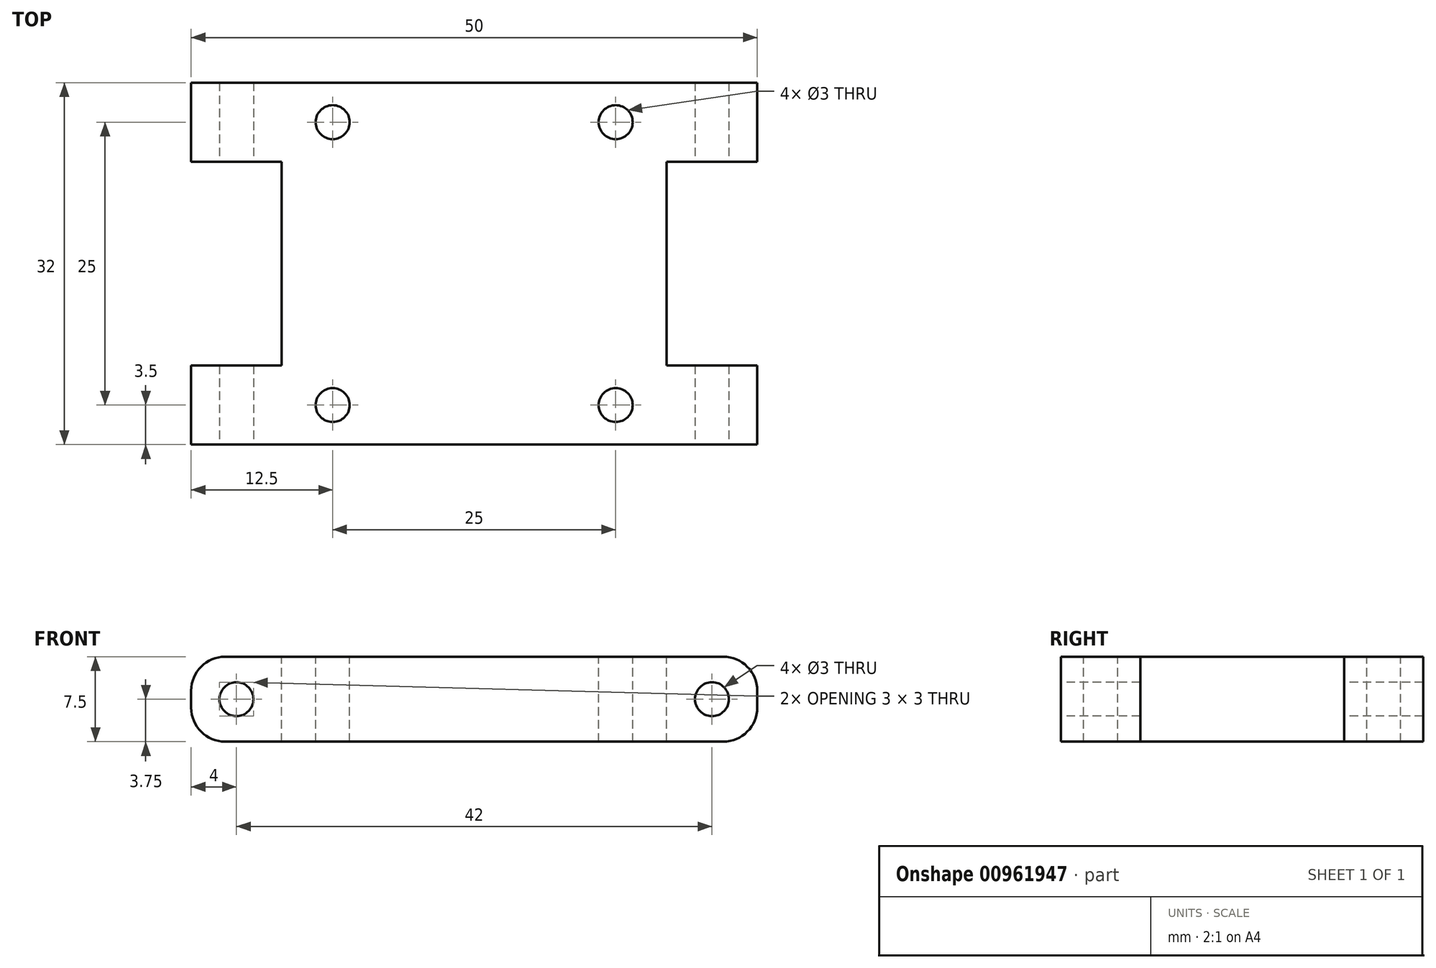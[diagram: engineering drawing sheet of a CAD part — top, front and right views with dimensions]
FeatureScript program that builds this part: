
annotation { "Feature Type Name" : "Feature", "Feature Type Description" : "" }
export const myFeature = defineFeature(function(context is Context, id is Id, definition is map)
    precondition{}
    {
        {
            var Q0;
            Q0=qCreatedBy(makeId("Top.planeOp"),FACE);
            var sketch = newSketch(context, id + "F0", { "sketchPlane" : qUnion([Q0])});
            skLineSegment(sketch, "E0.bottom", {"start": v(0, 0) * mm, "end": v(25, 0) * mm});
            skLineSegment(sketch, "E0.top", {"start": v(0, 32) * mm, "end": v(25, 32) * mm});
            skLineSegment(sketch, "E0.left", {"start": v(0, 0) * mm, "end": v(0, 32) * mm});
            skLineSegment(sketch, "E0.right", {"start": v(25, 0) * mm, "end": v(25, 32) * mm});
            skSolve(sketch);
        }
        {
            var Q0;
            Q0=makeQuery(id+"F0.imprint","IMPRINT",FACE,{"disambiguationData":[TD([[makeQuery(id+"F0.imprint","IMPRINT",EDGE,{"derivedFrom":sQuery(id+"F0.wireOp",EDGE,"E0.bottom")}),1.0]])]});
            extrude(context, id + "F1", {"entities" : qUnion([Q0]), "depth" : 7.5 * mm, "offsetDistance" : 25 * mm, "symmetric" : true});
        }
        {
            var Q0;
            Q0=qCreatedBy(makeId("Top.planeOp"),FACE);
            var sketch = newSketch(context, id + "F2", { "sketchPlane" : qUnion([Q0])});
            skLineSegment(sketch, "E1.bottom", {"start": v(29.2, 25) * mm, "end": v(17, 25) * mm});
            skLineSegment(sketch, "E1.top", {"start": v(29.2, 7) * mm, "end": v(17, 7) * mm});
            skLineSegment(sketch, "E1.left", {"start": v(29.2, 25) * mm, "end": v(29.2, 7) * mm});
            skLineSegment(sketch, "E1.right", {"start": v(17, 25) * mm, "end": v(17, 7) * mm});
            skSolve(sketch);
        }
        {
            var Q0;
            Q0=makeQuery(id+"F2.imprint","IMPRINT",FACE,{"disambiguationData":[TD([[makeQuery(id+"F2.imprint","IMPRINT",EDGE,{"derivedFrom":sQuery(id+"F2.wireOp",EDGE,"E1.bottom")}),1.0]])]});
            extrude(context, id + "F3", {"entities" : qUnion([Q0]), "operationType" : NewBodyOperationType.REMOVE, "oppositeDirection" : true, "depth" : 7.5 * mm, "offsetDistance" : 25 * mm, "symmetric" : true});
        }
        {
            var Q0;
            Q0=qCreatedBy(makeId("Front.planeOp"),FACE);
            var sketch = newSketch(context, id + "F4", { "sketchPlane" : qUnion([Q0])});
            skCircle(sketch, "E2", {"center": v(21, 0) * mm, "radius": 1.5 * mm});
            skSolve(sketch);
        }
        {
            var Q0;
            Q0=makeQuery(id+"F4.imprint","IMPRINT",FACE,{"disambiguationData":[TD([[makeQuery(id+"F4.imprint","IMPRINT",EDGE,{"derivedFrom":sQuery(id+"F4.wireOp",EDGE,"E2")}),1.0]])]});
            extrude(context, id + "F5", {"entities" : qUnion([Q0]), "operationType" : NewBodyOperationType.REMOVE, "oppositeDirection" : true, "depth" : 32 * mm, "offsetDistance" : 25 * mm});
        }
        {
            var Q0;
            {var subQ0=sQuery(id+"F0.wireOp",EDGE,"E0.right");var subQ1=sQuery(id+"F0.wireOp",EDGE,"E0.top");Q0=makeQuery(id+"F3.boolean.opBoolean","SPLIT",EDGE,{"disambiguationData":[TD([makeQuery(id+"F1.opExtrude","SWEPT_FACE",FACE,{"disambiguationData":[OSD([subQ1])]})])],"derivedFrom":makeQuery(id+"F1.opExtrude","CAP_EDGE",EDGE,{"disambiguationData":[OSD([subQ0])],"isStart":true})});}
            var Q1;
            {var subQ0=sQuery(id+"F0.wireOp",EDGE,"E0.right");var subQ1=sQuery(id+"F0.wireOp",EDGE,"E0.top");Q1=makeQuery(id+"F3.boolean.opBoolean","SPLIT",EDGE,{"disambiguationData":[TD([makeQuery(id+"F1.opExtrude","SWEPT_FACE",FACE,{"disambiguationData":[OSD([subQ1])]})])],"derivedFrom":makeQuery(id+"F1.opExtrude","CAP_EDGE",EDGE,{"disambiguationData":[OSD([subQ0])],"isStart":false})});}
            var Q2;
            {var subQ0=sQuery(id+"F0.wireOp",EDGE,"E0.bottom");var subQ1=sQuery(id+"F0.wireOp",EDGE,"E0.right");Q2=makeQuery(id+"F3.boolean.opBoolean","SPLIT",EDGE,{"disambiguationData":[TD([makeQuery(id+"F1.opExtrude","SWEPT_FACE",FACE,{"disambiguationData":[OSD([subQ0])]})])],"derivedFrom":makeQuery(id+"F1.opExtrude","CAP_EDGE",EDGE,{"disambiguationData":[OSD([subQ1])],"isStart":false})});}
            var Q3;
            {var subQ0=sQuery(id+"F0.wireOp",EDGE,"E0.bottom");var subQ1=sQuery(id+"F0.wireOp",EDGE,"E0.right");Q3=makeQuery(id+"F3.boolean.opBoolean","SPLIT",EDGE,{"disambiguationData":[TD([makeQuery(id+"F1.opExtrude","SWEPT_FACE",FACE,{"disambiguationData":[OSD([subQ0])]})])],"derivedFrom":makeQuery(id+"F1.opExtrude","CAP_EDGE",EDGE,{"disambiguationData":[OSD([subQ1])],"isStart":true})});}
            fillet(context, id + "F6", {"entities" : qUnion([Q0, Q1, Q2, Q3]), "radius" : 3 * mm, "tangentPropagation" : true, "allowEdgeOverflow" : false});
        }
        {
            var Q0;
            Q0=qCreatedBy(makeId("Top.planeOp"),FACE);
            var sketch = newSketch(context, id + "F7", { "sketchPlane" : qUnion([Q0])});
            skCircle(sketch, "E3", {"center": v(12.5, 3.5) * mm, "radius": 1.5 * mm});
            skCircle(sketch, "E4", {"center": v(12.5, 28.5) * mm, "radius": 1.5 * mm});
            skSolve(sketch);
        }
        {
            var Q0;
            Q0 = qSketchRegion(id + "F7", true);
            extrude(context, id + "F8", {"entities" : qUnion([Q0]), "operationType" : NewBodyOperationType.REMOVE, "oppositeDirection" : true, "depth" : 7.5 * mm, "offsetDistance" : 25 * mm, "symmetric" : true});
        }
        {
            var Q0;
            Q0=makeQuery(id+"F1.opExtrude","SWEPT_BODY",BODY,{"disambiguationData":[OSD([sQuery(id+"F0.wireOp",EDGE,"E0.bottom"),sQuery(id+"F0.wireOp",EDGE,"E0.top"),sQuery(id+"F0.wireOp",EDGE,"E0.left"),sQuery(id+"F0.wireOp",EDGE,"E0.right")])]});
            var Q1;
            Q1=qCreatedBy(makeId("Right.planeOp"),FACE);
            mirror(context, id + "F9", {"operationType" : NewBodyOperationType.ADD, "entities" : qUnion([Q0]), "mirrorPlane" : qUnion([Q1])});
        }
    });
